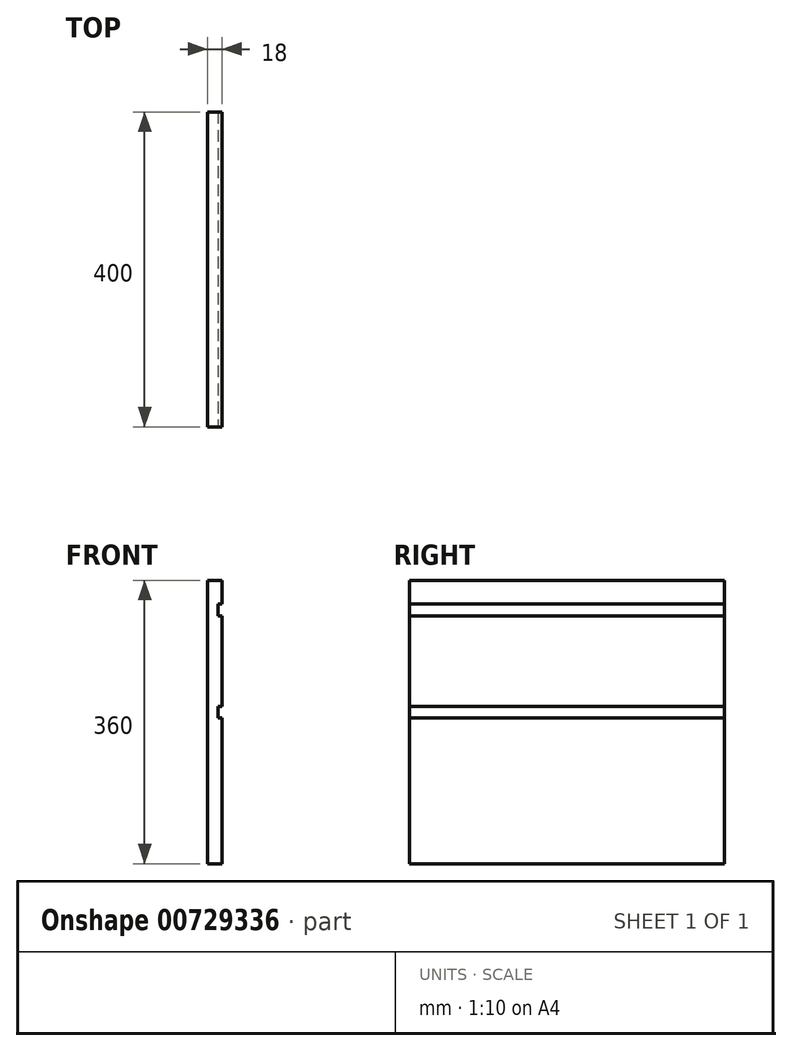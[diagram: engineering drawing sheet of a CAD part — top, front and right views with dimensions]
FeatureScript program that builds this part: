
annotation { "Feature Type Name" : "Feature", "Feature Type Description" : "" }
export const myFeature = defineFeature(function(context is Context, id is Id, definition is map)
    precondition{}
    {
        {
            var Q0;
            Q0=qCreatedBy(makeId("Front.planeOp"),FACE);
            var sketch = newSketch(context, id + "F0", { "sketchPlane" : qUnion([Q0])});
            skLineSegment(sketch, "E0.bottom", {"start": v(0, 0) * mm, "end": v(18, 0) * mm});
            skLineSegment(sketch, "E0.top", {"start": v(0, 360) * mm, "end": v(18, 360) * mm});
            skLineSegment(sketch, "E0.left", {"start": v(0, 0) * mm, "end": v(0, 360) * mm});
            skLineSegment(sketch, "E0.right", {"start": v(18, 0) * mm, "end": v(18, 360) * mm});
            skSolve(sketch);
        }
        {
            var Q0;
            Q0 = qSketchRegion(id + "F0", true);
            extrude(context, id + "F1", {"entities" : qUnion([Q0]), "oppositeDirection" : true, "depth" : 400 * mm, "offsetDistance" : 25 * mm});
        }
        {
            var Q0;
            Q0=makeQuery(id+"F1.opExtrude","CAP_FACE",FACE,{"disambiguationData":[OSD([sQuery(id+"F0.wireOp",EDGE,"E0.bottom"),sQuery(id+"F0.wireOp",EDGE,"E0.top"),sQuery(id+"F0.wireOp",EDGE,"E0.left"),sQuery(id+"F0.wireOp",EDGE,"E0.right")])],"isStart":true});
            var sketch = newSketch(context, id + "F2", { "sketchPlane" : qUnion([Q0])});
            skLineSegment(sketch, "E1.bottom", {"start": v(18, 185) * mm, "end": v(13, 185) * mm});
            skLineSegment(sketch, "E1.top", {"start": v(18, 200) * mm, "end": v(13, 200) * mm});
            skLineSegment(sketch, "E1.left", {"start": v(18, 185) * mm, "end": v(18, 200) * mm});
            skLineSegment(sketch, "E1.right", {"start": v(13, 185) * mm, "end": v(13, 200) * mm});
            skLineSegment(sketch, "E2.bottom", {"start": v(18, 330) * mm, "end": v(13, 330) * mm});
            skLineSegment(sketch, "E2.top", {"start": v(18, 315) * mm, "end": v(13, 315) * mm});
            skLineSegment(sketch, "E2.left", {"start": v(18, 330) * mm, "end": v(18, 315) * mm});
            skLineSegment(sketch, "E2.right", {"start": v(13, 330) * mm, "end": v(13, 315) * mm});
            skSolve(sketch);
        }
        {
            var Q0;
            Q0 = qSketchRegion(id + "F2", true);
            var Q1;
            Q1=makeQuery(id+"F1.opExtrude","CAP_FACE",FACE,{"disambiguationData":[OSD([sQuery(id+"F0.wireOp",EDGE,"E0.bottom"),sQuery(id+"F0.wireOp",EDGE,"E0.top"),sQuery(id+"F0.wireOp",EDGE,"E0.left"),sQuery(id+"F0.wireOp",EDGE,"E0.right")])],"isStart":false});
            extrude(context, id + "F3", {"entities" : qUnion([Q0]), "operationType" : NewBodyOperationType.REMOVE, "endBound" : BoundingType.THROUGH_ALL, "oppositeDirection" : true, "depth" : 25 * mm, "endBoundEntityFace" : qUnion([Q1]), "offsetDistance" : 25 * mm});
        }
    });
